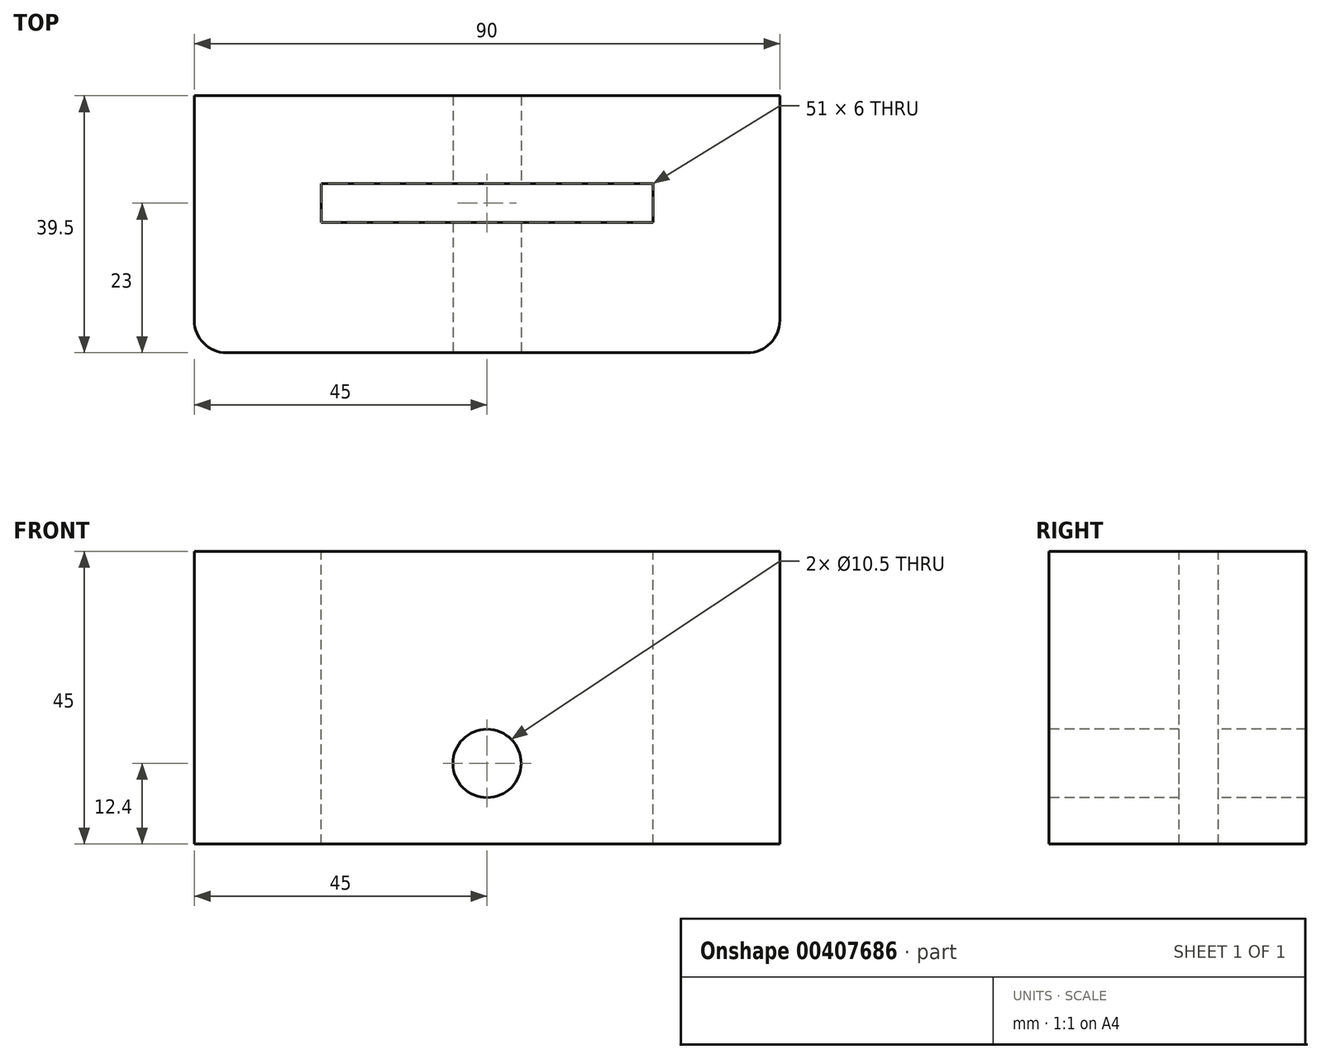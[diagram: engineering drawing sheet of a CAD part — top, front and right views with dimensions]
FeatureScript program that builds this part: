
annotation { "Feature Type Name" : "Feature", "Feature Type Description" : "" }
export const myFeature = defineFeature(function(context is Context, id is Id, definition is map)
    precondition{}
    {
        {
            var Q0;
            Q0=qCreatedBy(makeId("Top.planeOp"),FACE);
            var sketch = newSketch(context, id + "F0", { "sketchPlane" : qUnion([Q0])});
            skLineSegment(sketch, "E0.bottom", {"start": v(45, 19.75) * mm, "end": v(-45, 19.75) * mm});
            skLineSegment(sketch, "E0.top", {"start": v(45, -19.75) * mm, "end": v(-45, -19.75) * mm});
            skLineSegment(sketch, "E0.left", {"start": v(45, 19.75) * mm, "end": v(45, -19.75) * mm});
            skLineSegment(sketch, "E0.right", {"start": v(-45, 19.75) * mm, "end": v(-45, -19.75) * mm});
            skPoint(sketch, "E0.middle", {"position": v(0, 0) * mm});
            skSolve(sketch);
        }
        {
            var Q0;
            Q0=makeQuery(id+"F0.imprint","IMPRINT",FACE,{"disambiguationData":[TD([[makeQuery(id+"F0.imprint","IMPRINT",EDGE,{"derivedFrom":sQuery(id+"F0.wireOp",EDGE,"E0.bottom")}),1.0]])]});
            extrude(context, id + "F1", {"entities" : qUnion([Q0]), "depth" : 45 * mm});
        }
        {
            var Q0;
            Q0=makeQuery(id+"F1.opExtrude","SWEPT_FACE",FACE,{"disambiguationData":[OSD([sQuery(id+"F0.wireOp",EDGE,"E0.top")])]});
            var sketch = newSketch(context, id + "F2", { "sketchPlane" : qUnion([Q0])});
            skCircle(sketch, "E1", {"center": v(0, 12.4) * mm, "radius": 5.25 * mm});
            skPoint(sketch, "E1.centerSnap0", {"position": v(0, 0) * mm});
            skSolve(sketch);
        }
        {
            var Q0;
            Q0=makeQuery(id+"F2.imprint","IMPRINT",FACE,{"disambiguationData":[TD([[makeQuery(id+"F2.imprint","IMPRINT",EDGE,{"derivedFrom":sQuery(id+"F2.wireOp",EDGE,"E1")}),1.0]])]});
            var Q1;
            Q1=makeQuery(id+"F1.opExtrude","SWEPT_FACE",FACE,{"disambiguationData":[OSD([sQuery(id+"F0.wireOp",EDGE,"E0.bottom")])]});
            extrude(context, id + "F3", {"entities" : qUnion([Q0]), "operationType" : NewBodyOperationType.REMOVE, "endBound" : BoundingType.UP_TO_SURFACE, "oppositeDirection" : true, "endBoundEntityFace" : qUnion([Q1]), "depth" : 25 * mm});
        }
        {
            var Q0;
            Q0=makeQuery(id+"F1.opExtrude","CAP_FACE",FACE,{"disambiguationData":[OSD([sQuery(id+"F0.wireOp",EDGE,"E0.bottom"),sQuery(id+"F0.wireOp",EDGE,"E0.top"),sQuery(id+"F0.wireOp",EDGE,"E0.left"),sQuery(id+"F0.wireOp",EDGE,"E0.right")])],"isStart":false});
            var sketch = newSketch(context, id + "F4", { "sketchPlane" : qUnion([Q0])});
            skLineSegment(sketch, "E2.0", {"start": v(45, 19.75) * mm, "end": v(-45, 19.75) * mm, "construction": true});
            skLineSegment(sketch, "E3.0", {"start": v(45, -19.75) * mm, "end": v(-45, -19.75) * mm, "construction": true});
            skLineSegment(sketch, "E4", {"start": v(0, 19.75) * mm, "end": v(0, -19.75) * mm, "construction": true});
            skLineSegment(sketch, "E5", {"start": v(0, 6.25) * mm, "end": v(25.5, 6.25) * mm});
            skLineSegment(sketch, "E6", {"start": v(25.5, 6.25) * mm, "end": v(25.5, 0.25) * mm});
            skLineSegment(sketch, "E7", {"start": v(25.5, 0.25) * mm, "end": v(0, 0.25) * mm});
            skLineSegment(sketch, "E8.MirrorCS", {"start": v(0, 6.25) * mm, "end": v(-25.5, 6.25) * mm});
            skLineSegment(sketch, "E9.MirrorCS", {"start": v(-25.5, 6.25) * mm, "end": v(-25.5, 0.25) * mm});
            skLineSegment(sketch, "E10.MirrorCS", {"start": v(-25.5, 0.25) * mm, "end": v(0, 0.25) * mm});
            skSolve(sketch);
        }
        {
            var Q0;
            Q0=makeQuery(id+"F4.imprint","IMPRINT",FACE,{"disambiguationData":[TD([[makeQuery(id+"F4.imprint","IMPRINT",EDGE,{"derivedFrom":sQuery(id+"F4.wireOp",EDGE,"E5")}),-1.0]])]});
            extrude(context, id + "F5", {"entities" : qUnion([Q0]), "operationType" : NewBodyOperationType.REMOVE, "endBound" : BoundingType.THROUGH_ALL, "oppositeDirection" : true, "depth" : 25 * mm});
        }
        {
            var Q0;
            Q0=makeQuery(id+"F1.opExtrude","SWEPT_EDGE",EDGE,{"disambiguationData":[OSD([sQuery(id+"F0.wireOp",EDGE,"E0.top"),sQuery(id+"F0.wireOp",EDGE,"E0.right")])]});
            var Q1;
            Q1=makeQuery(id+"F1.opExtrude","SWEPT_EDGE",EDGE,{"disambiguationData":[OSD([sQuery(id+"F0.wireOp",EDGE,"E0.top"),sQuery(id+"F0.wireOp",EDGE,"E0.left")])]});
            fillet(context, id + "F6", {"entities" : qUnion([Q0, Q1]), "radius" : 5 * mm, "tangentPropagation" : true, "allowEdgeOverflow" : false});
        }
    });
